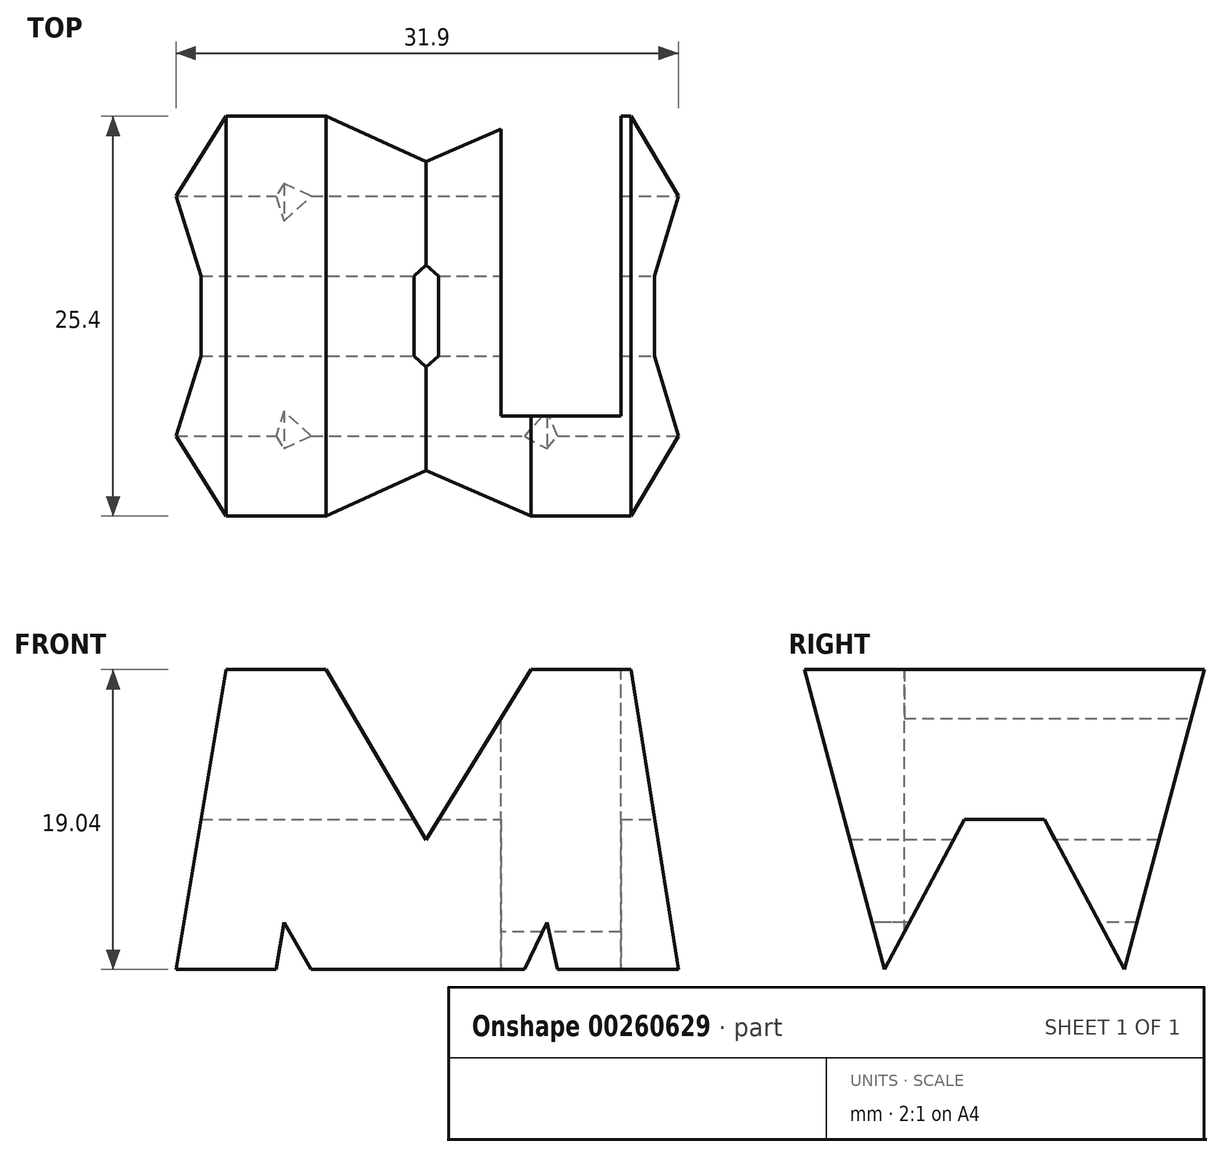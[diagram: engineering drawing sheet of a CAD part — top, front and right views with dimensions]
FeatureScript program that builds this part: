
annotation { "Feature Type Name" : "Feature", "Feature Type Description" : "" }
export const myFeature = defineFeature(function(context is Context, id is Id, definition is map)
    precondition{}
    {
        {
            var Q0;
            Q0=qCreatedBy(makeId("Front.planeOp"),FACE);
            var sketch = newSketch(context, id + "F0", { "sketchPlane" : qUnion([Q0])});
            skLineSegment(sketch, "E0", {"start": v(28.41, 38.1) * mm, "end": v(28.41, 0) * mm});
            skLineSegment(sketch, "E1", {"start": v(28.41, 38.1) * mm, "end": v(66.51, 38.1) * mm});
            skLineSegment(sketch, "E2", {"start": v(66.51, 38.1) * mm, "end": v(66.51, 0) * mm});
            skLineSegment(sketch, "E3", {"start": v(28.41, 0) * mm, "end": v(66.51, 0) * mm});
            skSolve(sketch);
        }
        {
            var Q0;
            Q0=makeQuery(id+"F0.imprint","IMPRINT",FACE,{"disambiguationData":[TD([[makeQuery(id+"F0.imprint","IMPRINT",EDGE,{"derivedFrom":sQuery(id+"F0.wireOp",EDGE,"E0")}),1.0]])]});
            extrude(context, id + "F1", {"entities" : qUnion([Q0]), "depth" : 38.1 * mm});
        }
        {
            var Q0;
            Q0=qCreatedBy(makeId("Front.planeOp"),FACE);
            cPlane(context, id + "F2", {"entities" : qUnion([Q0]), "cplaneType" : CPlaneType.OFFSET, "offset" : 38.1 * mm, "width" : 152.4 * mm, "height" : 152.4 * mm});
        }
        {
            var Q0;
            Q0=qCreatedBy(makeId("Top.planeOp"),FACE);
            var Q1;
            Q1 = qBodyType(qCreatedBy(id + "F4" ,EDGE), BodyType.WIRE);
            cPlane(context, id + "F3", {"entities" : qUnion([Q0, Q1]), "cplaneType" : CPlaneType.OFFSET, "offset" : 38.1 * mm, "width" : 152.4 * mm, "height" : 152.4 * mm});
        }
        {
            var Q0;
            Q0=makeQuery(id+"F1.opExtrude","SWEPT_FACE",FACE,{"disambiguationData":[OSD([sQuery(id+"F0.wireOp",EDGE,"E2")])]});
            var sketch = newSketch(context, id + "F4", { "sketchPlane" : qUnion([Q0])});
            skLineSegment(sketch, "E4", {"start": v(-38.1, 38.1) * mm, "end": v(-38.1, 0) * mm});
            skLineSegment(sketch, "E5", {"start": v(0, 0) * mm, "end": v(0, 38.1) * mm});
            skLineSegment(sketch, "E6", {"start": v(0, 38.1) * mm, "end": v(-38.1, 38.1) * mm});
            skLineSegment(sketch, "E7", {"start": v(-38.1, 38.1) * mm, "end": v(-31.75, 0) * mm});
            skLineSegment(sketch, "E8", {"start": v(-31.75, 38.1) * mm, "end": v(-26.67, 19.06) * mm});
            skLineSegment(sketch, "E9", {"start": v(-11.43, 19.06) * mm, "end": v(-6.35, 38.1) * mm});
            skLineSegment(sketch, "E10", {"start": v(0, 38.1) * mm, "end": v(-6.35, 0) * mm});
            skLineSegment(sketch, "E11", {"start": v(-38.1, 38.1) * mm, "end": v(-31.75, 38.1) * mm});
            skLineSegment(sketch, "E12", {"start": v(-6.35, 38.1) * mm, "end": v(0, 38.1) * mm});
            skLineSegment(sketch, "E13", {"start": v(0, 38.1) * mm, "end": v(0, 38.1) * mm});
            skLineSegment(sketch, "E14", {"start": v(-25.4, 0) * mm, "end": v(-31.75, 0) * mm});
            skLineSegment(sketch, "E15", {"start": v(-12.7, 0) * mm, "end": v(-6.35, 0) * mm});
            skLineSegment(sketch, "E16", {"start": v(-38.1, 0) * mm, "end": v(0, 0) * mm});
            skLineSegment(sketch, "E17", {"start": v(-26.67, 19.06) * mm, "end": v(-21.59, 28.58) * mm});
            skLineSegment(sketch, "E18", {"start": v(-21.59, 28.58) * mm, "end": v(-16.5, 28.58) * mm});
            skLineSegment(sketch, "E19", {"start": v(-16.5, 28.58) * mm, "end": v(-11.43, 19.06) * mm});
            skPoint(sketch, "E20.end.orphan", {"position": v(-19.05, 15.88) * mm});
            skLineSegment(sketch, "E21", {"start": v(-25.4, 0) * mm, "end": v(-19.05, 15.88) * mm});
            skLineSegment(sketch, "E22", {"start": v(-19.05, 15.88) * mm, "end": v(-12.7, 0) * mm});
            skSolve(sketch);
        }
        {
            var Q0;
            {var subQ0=sQuery(id+"F4.wireOp",EDGE,"E4");Q0=makeQuery(id+"F4.imprint","IMPRINT",FACE,{"disambiguationData":[TD([[makeQuery(id+"F4.imprint","IMPRINT",EDGE,{"derivedFrom":subQ0}),1.0]])]});}
            var Q1;
            Q1=makeQuery(id+"F4.imprint","IMPRINT",FACE,{"disambiguationData":[TD([[makeQuery(id+"F4.imprint","IMPRINT",EDGE,{"derivedFrom":sQuery(id+"F4.wireOp",EDGE,"E6")}),-1.0]])]});
            var Q2;
            {var subQ0=sQuery(id+"F4.wireOp",EDGE,"E5");Q2=makeQuery(id+"F4.imprint","IMPRINT",FACE,{"disambiguationData":[TD([[makeQuery(id+"F4.imprint","IMPRINT",EDGE,{"derivedFrom":subQ0}),-1.0]])]});}
            var Q3;
            {var subQ0=sQuery(id+"F4.wireOp",EDGE,"E21");Q3=makeQuery(id+"F4.imprint","IMPRINT",FACE,{"disambiguationData":[TD([[makeQuery(id+"F4.imprint","IMPRINT",EDGE,{"derivedFrom":subQ0}),-1.0]])]});}
            extrude(context, id + "F5", {"entities" : qUnion([Q0, Q1, Q2, Q3]), "operationType" : NewBodyOperationType.REMOVE, "oppositeDirection" : true, "depth" : 38.1 * mm});
        }
        {
            var Q0;
            Q0=qCreatedBy(id+"F2.planeOp",FACE);
            var sketch = newSketch(context, id + "F6", { "sketchPlane" : qUnion([Q0])});
            skLineSegment(sketch, "E23", {"start": v(28.41, 38.1) * mm, "end": v(28.41, 0) * mm});
            skLineSegment(sketch, "E24", {"start": v(28.41, 0) * mm, "end": v(66.51, 0) * mm});
            skLineSegment(sketch, "E25", {"start": v(66.51, 0) * mm, "end": v(66.51, 38.1) * mm});
            skLineSegment(sketch, "E26", {"start": v(28.41, 38.1) * mm, "end": v(66.51, 38.1) * mm});
            skLineSegment(sketch, "E27", {"start": v(28.41, 0) * mm, "end": v(34.76, 38.1) * mm});
            skLineSegment(sketch, "E28", {"start": v(41.11, 38.1) * mm, "end": v(47.46, 27.28) * mm});
            skPoint(sketch, "E29.end.orphan", {"position": v(66.51, 17.45) * mm});
            skLineSegment(sketch, "E30", {"start": v(60.48, 38.1) * mm, "end": v(66.51, 0) * mm});
            skLineSegment(sketch, "E31", {"start": v(54.13, 38.1) * mm, "end": v(54.13, 38.1) * mm});
            skLineSegment(sketch, "E32", {"start": v(47.46, 27.28) * mm, "end": v(54.13, 38.1) * mm});
            skPoint(sketch, "E33.end.orphan", {"position": v(60.16, 0) * mm});
            skPoint(sketch, "E34.start.orphan", {"position": v(34.76, 0) * mm});
            skPoint(sketch, "E35.end.orphan", {"position": v(52.62, 21.58) * mm});
            skLineSegment(sketch, "E36", {"start": v(34.76, 0) * mm, "end": v(38.44, 22.05) * mm});
            skLineSegment(sketch, "E37", {"start": v(38.44, 22.05) * mm, "end": v(44.15, 12.22) * mm});
            skLineSegment(sketch, "E38", {"start": v(44.15, 12.22) * mm, "end": v(50.46, 12.22) * mm});
            skLineSegment(sketch, "E39", {"start": v(50.46, 12.22) * mm, "end": v(55.14, 22.05) * mm});
            skLineSegment(sketch, "E40", {"start": v(55.14, 22.05) * mm, "end": v(60.16, 0) * mm});
            skSolve(sketch);
        }
        {
            var Q0;
            {var subQ0=sQuery(id+"F6.wireOp",EDGE,"E36");Q0=makeQuery(id+"F6.imprint","IMPRINT",FACE,{"disambiguationData":[TD([[makeQuery(id+"F6.imprint","IMPRINT",EDGE,{"derivedFrom":subQ0}),-1.0]])]});}
            var Q1;
            {var subQ0=sQuery(id+"F6.wireOp",EDGE,"E23");Q1=makeQuery(id+"F6.imprint","IMPRINT",FACE,{"disambiguationData":[TD([[makeQuery(id+"F6.imprint","IMPRINT",EDGE,{"derivedFrom":subQ0}),1.0]])]});}
            var Q2;
            {var subQ0=sQuery(id+"F6.wireOp",EDGE,"E28");Q2=makeQuery(id+"F6.imprint","IMPRINT",FACE,{"disambiguationData":[TD([[makeQuery(id+"F6.imprint","IMPRINT",EDGE,{"derivedFrom":subQ0}),1.0]])]});}
            var Q3;
            {var subQ0=sQuery(id+"F6.wireOp",EDGE,"E25");Q3=makeQuery(id+"F6.imprint","IMPRINT",FACE,{"disambiguationData":[TD([[makeQuery(id+"F6.imprint","IMPRINT",EDGE,{"derivedFrom":subQ0}),1.0]])]});}
            extrude(context, id + "F7", {"entities" : qUnion([Q0, Q1, Q2, Q3]), "operationType" : NewBodyOperationType.REMOVE, "oppositeDirection" : true, "depth" : 38.1 * mm});
        }
        {
            var Q0;
            Q0=qCreatedBy(id+"F3.planeOp",FACE);
            var sketch = newSketch(context, id + "F8", { "sketchPlane" : qUnion([Q0])});
            skLineSegment(sketch, "E41", {"start": v(29.36, 0) * mm, "end": v(67.46, 0) * mm});
            skLineSegment(sketch, "E42", {"start": v(67.46, 0) * mm, "end": v(67.46, -38.1) * mm});
            skLineSegment(sketch, "E43", {"start": v(67.46, -38.1) * mm, "end": v(44.6, -38.1) * mm});
            skLineSegment(sketch, "E44", {"start": v(29.36, 0) * mm, "end": v(29.14, -38.1) * mm});
            skLineSegment(sketch, "E45", {"start": v(36.98, -38.1) * mm, "end": v(36.98, -12.7) * mm});
            skLineSegment(sketch, "E46", {"start": v(36.98, -12.7) * mm, "end": v(44.6, -12.7) * mm});
            skLineSegment(sketch, "E47", {"start": v(44.6, -12.7) * mm, "end": v(44.6, -38.1) * mm});
            skLineSegment(sketch, "E48", {"start": v(52.22, 0) * mm, "end": v(52.22, -12.7) * mm});
            skLineSegment(sketch, "E49", {"start": v(59.84, -12.7) * mm, "end": v(59.84, 0) * mm});
            skLineSegment(sketch, "E50", {"start": v(52.22, -12.7) * mm, "end": v(52.22, -25.4) * mm});
            skLineSegment(sketch, "E51", {"start": v(59.84, -12.7) * mm, "end": v(59.84, -25.4) * mm});
            skLineSegment(sketch, "E52", {"start": v(52.22, -25.4) * mm, "end": v(59.84, -25.4) * mm});
            skSolve(sketch);
        }
        {
            var Q0;
            {var subQ0=sQuery(id+"F8.wireOp",EDGE,"E45");Q0=makeQuery(id+"F8.imprint","IMPRINT",FACE,{"disambiguationData":[TD([[makeQuery(id+"F8.imprint","IMPRINT",EDGE,{"derivedFrom":subQ0}),-1.0]])]});}
            var Q1;
            {var subQ1=sQuery(id+"F8.wireOp",EDGE,"E48");Q1=makeQuery(id+"F8.imprint","IMPRINT",FACE,{"disambiguationData":[TD([[makeQuery(id+"F8.imprint","IMPRINT",EDGE,{"derivedFrom":subQ1}),1.0]])]});}
            extrude(context, id + "F9", {"entities" : qUnion([Q0, Q1]), "operationType" : NewBodyOperationType.REMOVE, "oppositeDirection" : true, "depth" : 38.1 * mm});
        }
    });
